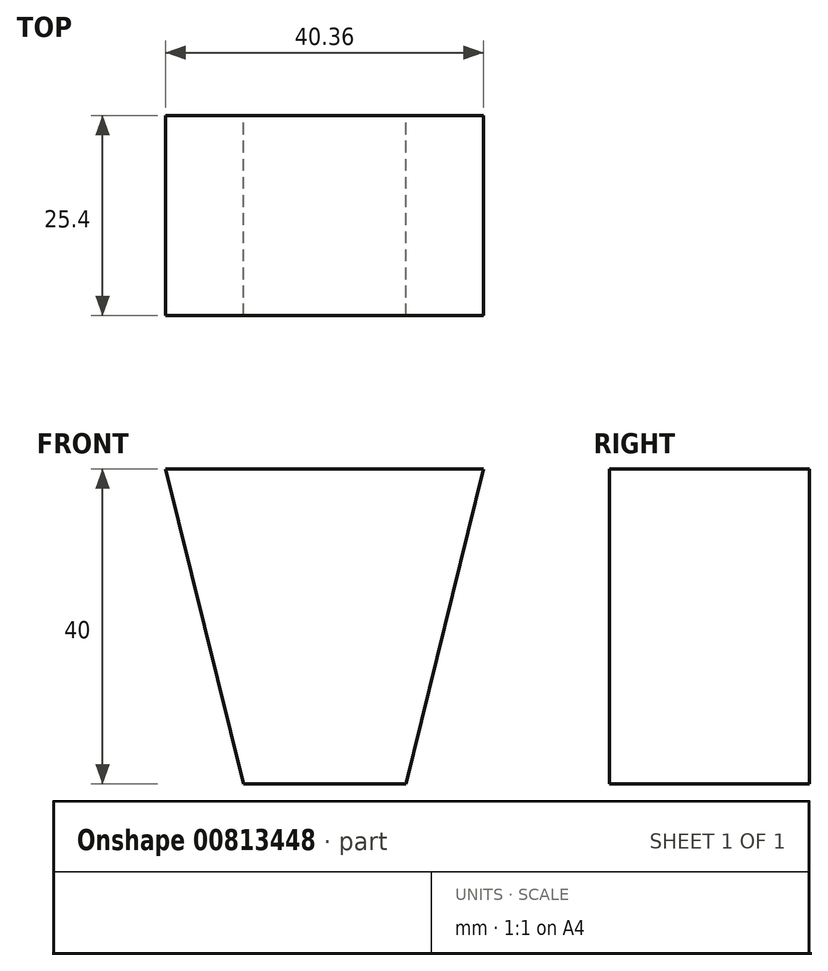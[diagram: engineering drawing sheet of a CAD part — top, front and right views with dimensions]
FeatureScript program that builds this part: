
annotation { "Feature Type Name" : "Feature", "Feature Type Description" : "" }
export const myFeature = defineFeature(function(context is Context, id is Id, definition is map)
    precondition{}
    {
        {
            var Q0;
            Q0=qCreatedBy(makeId("Front.planeOp"),FACE);
            var sketch = newSketch(context, id + "F0", { "sketchPlane" : qUnion([Q0])});
            skLineSegment(sketch, "E0", {"start": v(-20.18, 20) * mm, "end": v(20.18, 20) * mm});
            skLineSegment(sketch, "E1", {"start": v(20.18, 20) * mm, "end": v(10.32, -20) * mm});
            skLineSegment(sketch, "E2", {"start": v(10.32, -20) * mm, "end": v(-10.32, -20) * mm});
            skLineSegment(sketch, "E3", {"start": v(-10.32, -20) * mm, "end": v(-20.18, 20) * mm});
            skSolve(sketch);
        }
        {
            var Q0;
            Q0 = qSketchRegion(id + "F0", true);
            extrude(context, id + "F1", {"entities" : qUnion([Q0]), "endBound" : BoundingType.SYMMETRIC, "depth" : 25.4 * mm, "offsetDistance" : 25.4 * mm});
        }
    });
